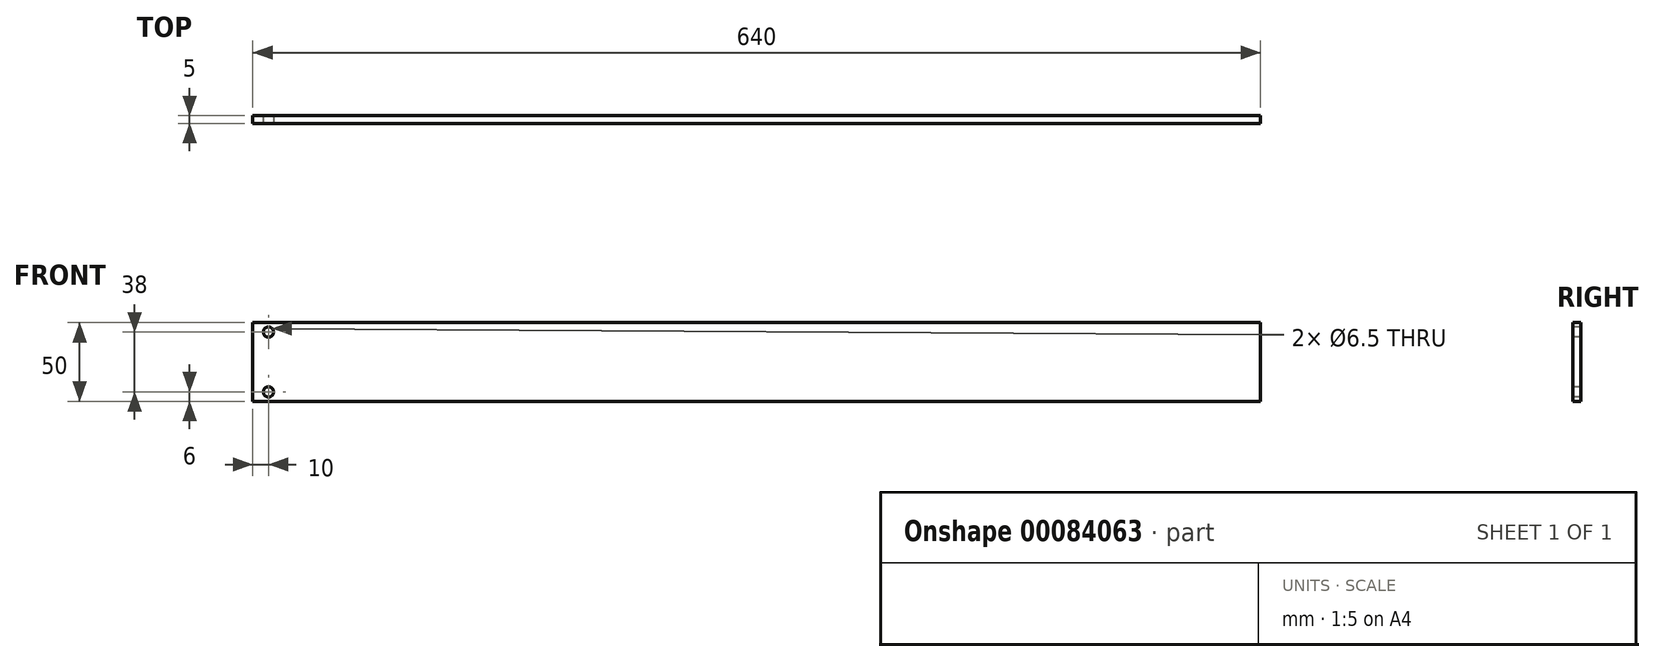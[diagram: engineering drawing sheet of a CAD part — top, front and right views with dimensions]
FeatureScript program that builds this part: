
annotation { "Feature Type Name" : "Feature", "Feature Type Description" : "" }
export const myFeature = defineFeature(function(context is Context, id is Id, definition is map)
    precondition{}
    {
        {
            var Q0;
            Q0=qCreatedBy(makeId("Front.planeOp"),FACE);
            var sketch = newSketch(context, id + "F0", { "sketchPlane" : qUnion([Q0])});
            skLineSegment(sketch, "E0.bottom", {"start": v(0, 0) * mm, "end": v(640, 0) * mm});
            skLineSegment(sketch, "E0.top", {"start": v(0, 50) * mm, "end": v(640, 50) * mm});
            skLineSegment(sketch, "E0.left", {"start": v(0, 0) * mm, "end": v(0, 50) * mm});
            skLineSegment(sketch, "E0.right", {"start": v(640, 0) * mm, "end": v(640, 50) * mm});
            skCircle(sketch, "E1", {"center": v(10, 44) * mm, "radius": 3.25 * mm});
            skCircle(sketch, "E2", {"center": v(10, 6) * mm, "radius": 3.25 * mm});
            skSolve(sketch);
        }
        {
            var Q0;
            Q0=makeQuery(id+"F0.imprint","IMPRINT",FACE,{"disambiguationData":[TD([[makeQuery(id+"F0.imprint","IMPRINT",EDGE,{"derivedFrom":sQuery(id+"F0.wireOp",EDGE,"E0.bottom")}),1.0]])]});
            extrude(context, id + "F1", {"entities" : qUnion([Q0]), "oppositeDirection" : true, "depth" : 5 * mm});
        }
    });
